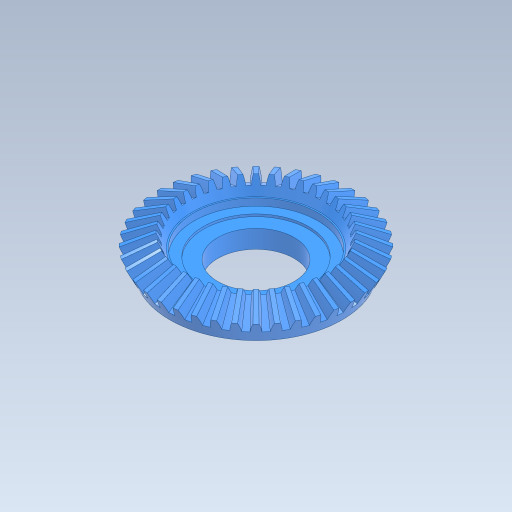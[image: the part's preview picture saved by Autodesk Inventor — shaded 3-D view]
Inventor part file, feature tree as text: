
AUTODESK INVENTOR PART (.ipt)
format: ipt  version: 2024 (Build 280153000, 153)  size: 747,008 bytes
history: native  units: mm
features: other x4, revolve x3, sketch x2, hole x1, extrude x1
ambient origin geometry x8: Origin, YZ Plane, XZ Plane, XY Plane, X Axis, Y Axis, Z Axis, Center Point
bodies: Solid1_1 (feature_tree)
feature tree (11):
  other  "_PB1-4020_On.ipt"
  sketch  "スケッチ1"
  revolve  "回転1"
  sketch  "スケッチ3"
  hole  "穴1"  [1 undecoded]
  revolve  "回転2"
  revolve  "回転3"
  extrude  "押し出し1"  Depth=10.0mm
  other  "厚み1"
  other  "Solid1::_PB1-4020_On.ipt"
  other  "TaggingFeature2"
note: 1 required parameter value undecoded (feature->parameter linkage not recoverable at this tier; creation-order binding heuristic only, values carry confidence <= 0.55)
